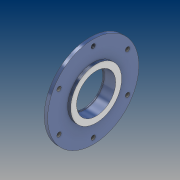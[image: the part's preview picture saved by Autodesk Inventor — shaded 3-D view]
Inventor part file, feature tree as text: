
AUTODESK INVENTOR PART (.ipt)
format: ipt  version: 2021 (Build 250183000, 183)  size: 174,592 bytes
history: native  units: mm
features: extrude x6, thread x6, sketch x6, plane x1
ambient origin geometry x8: Origin, YZ Plane, XZ Plane, XY Plane, X Axis, Y Axis, Z Axis, Center Point
bodies: Solid1 (feature_tree)
feature tree (19):
  extrude  "Extrusion1"  Depth=406.5mm
  extrude  "Extrusion2"  Depth=25.0mm
  plane  "Work Plane1"
  extrude  "Extrusion3"  Depth=20.0mm
  extrude  "Extrusion4"  Depth=70.0mm TaperAngle=0.0deg
  extrude  "Extrusion6"  Depth=10.0mm
  thread  "Thread20"  [1 undecoded]
  extrude  "Extrusion8"  Depth=20.0mm
  thread  "Thread30"  [1 undecoded]
  thread  "Thread31"  [1 undecoded]
  thread  "Thread32"  [1 undecoded]
  thread  "Thread33"  [1 undecoded]
  thread  "Thread34"  [1 undecoded]
  sketch  "Sketch1"  dims[d0=536.0mm d1=406.5mm]
  sketch  "Sketch2"  dims[d2=465.0mm d3=25.0mm]
  sketch  "Sketch3"  dims[d8=20.0mm d9=0.0mm d10=230.0mm]
  sketch  "Sketch4"  dims[d11=300.0mm d12=70.0mm d13=0.0mm]
  sketch  "Sketch6"  dims[d14=10.0mm d15=406.5mm d16=300.0mm]
  sketch  "Sketch9"  dims[d17=30.0mm d18=0.0mm d43=222.0mm d44=230.0mm d45=6.0mm d46=0.0mm d51=2.07mm d52=0.0mm d61=300.0mm d77=20.0mm d78=0.0mm d97=5.0mm d98=0.0mm d99=60.0mm d101=360.0deg d103=20.0mm d104=0.0mm d105=20.0mm d106=0.0mm d107=20.0mm d108=0.0mm d109=20.0mm d110=0.0mm d111=20.0mm d112=0.0mm d47=0.5mm d48=0.872665mm d49=0.5mm d50=0.872665mm d100=0.872665mm d102=0.872665mm]
note: 6 required parameter values undecoded (feature->parameter linkage not recoverable at this tier; creation-order binding heuristic only, values carry confidence <= 0.55)
